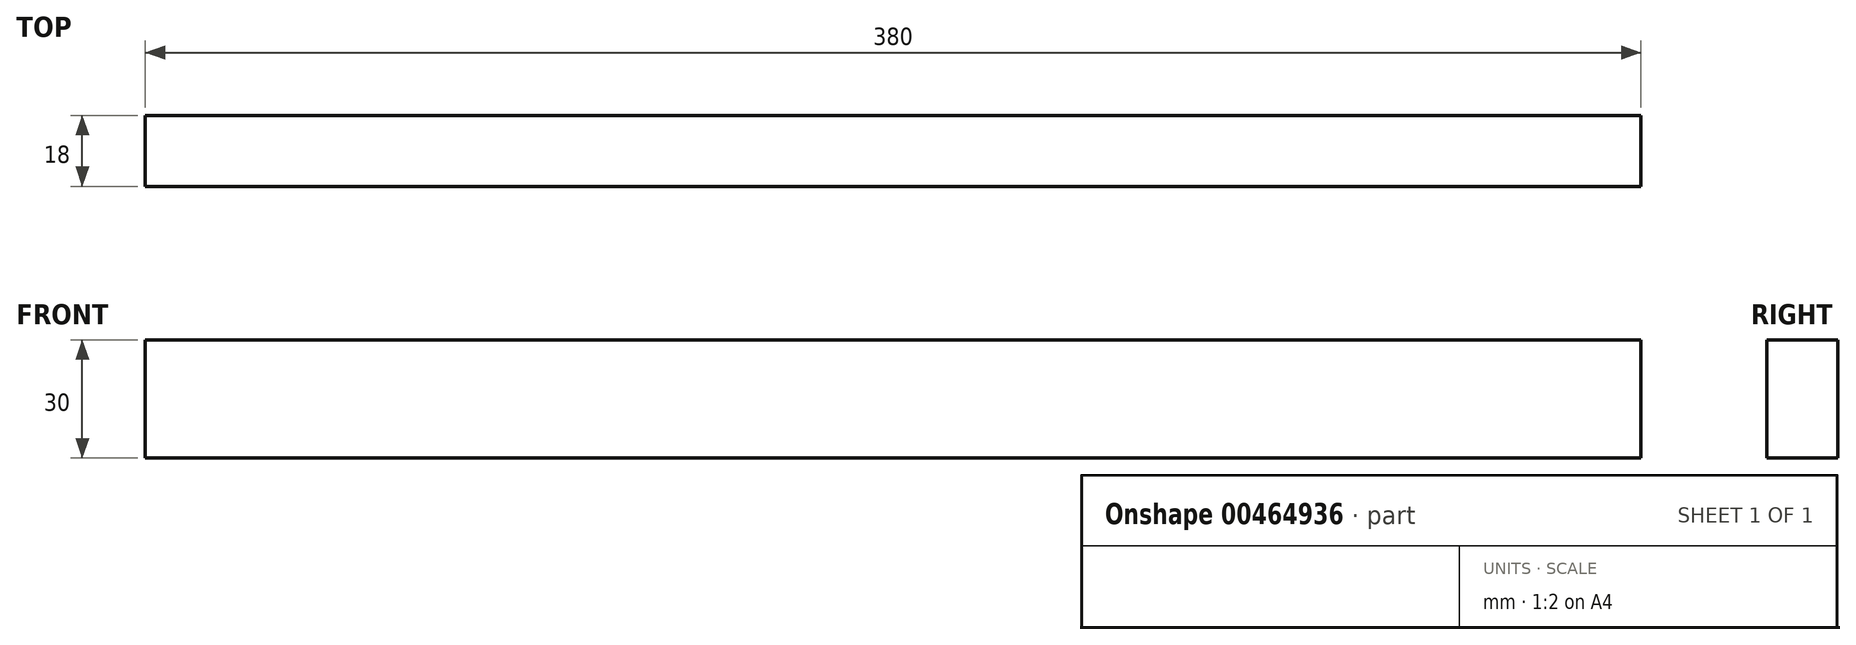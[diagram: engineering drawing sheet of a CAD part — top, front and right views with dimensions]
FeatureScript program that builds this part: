
annotation { "Feature Type Name" : "Feature", "Feature Type Description" : "" }
export const myFeature = defineFeature(function(context is Context, id is Id, definition is map)
    precondition{}
    {
        {
            var Q0;
            Q0=qCreatedBy(makeId("Right.planeOp"),FACE);
            var sketch = newSketch(context, id + "F0", { "sketchPlane" : qUnion([Q0])});
            skLineSegment(sketch, "E0.bottom", {"start": v(-9, 15) * mm, "end": v(9, 15) * mm});
            skLineSegment(sketch, "E0.top", {"start": v(-9, -15) * mm, "end": v(9, -15) * mm});
            skLineSegment(sketch, "E0.left", {"start": v(-9, 15) * mm, "end": v(-9, -15) * mm});
            skLineSegment(sketch, "E0.right", {"start": v(9, 15) * mm, "end": v(9, -15) * mm});
            skPoint(sketch, "E0.middle", {"position": v(0, 0) * mm});
            skSolve(sketch);
        }
        {
            var Q0;
            Q0=makeQuery(id+"F0.imprint","IMPRINT",FACE,{"disambiguationData":[TD([[makeQuery(id+"F0.imprint","IMPRINT",EDGE,{"derivedFrom":sQuery(id+"F0.wireOp",EDGE,"E0.bottom")}),-1.0]])]});
            extrude(context, id + "F1", {"entities" : qUnion([Q0]), "endBound" : BoundingType.SYMMETRIC, "depth" : 380 * mm, "offsetDistance" : 25 * mm});
        }
    });
